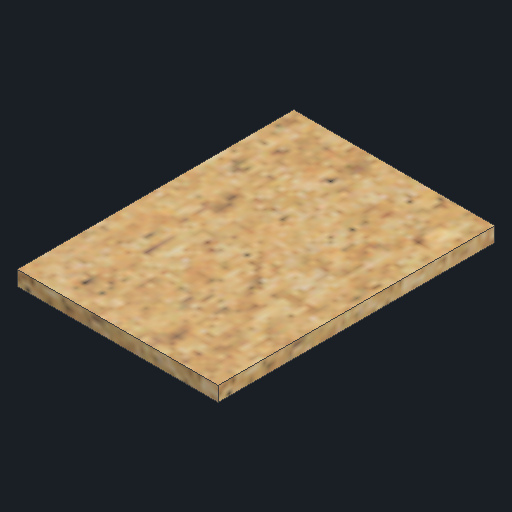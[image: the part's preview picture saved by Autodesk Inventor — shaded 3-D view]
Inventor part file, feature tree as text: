
AUTODESK INVENTOR PART (.ipt)
format: ipt  version: 2022 (Build 260153070, 153G)  size: 249,856 bytes
history: native  units: mm
features: extrude x1, sketch x1
ambient origin geometry x8: Origin, YZ Plane, XZ Plane, XY Plane, X Axis, Y Axis, Z Axis, Center Point
bodies: Body1 (feature_tree)
feature tree (2):
  extrude  "Выдавливание2"  Depth=218.0mm
  sketch  "Эскиз3"
